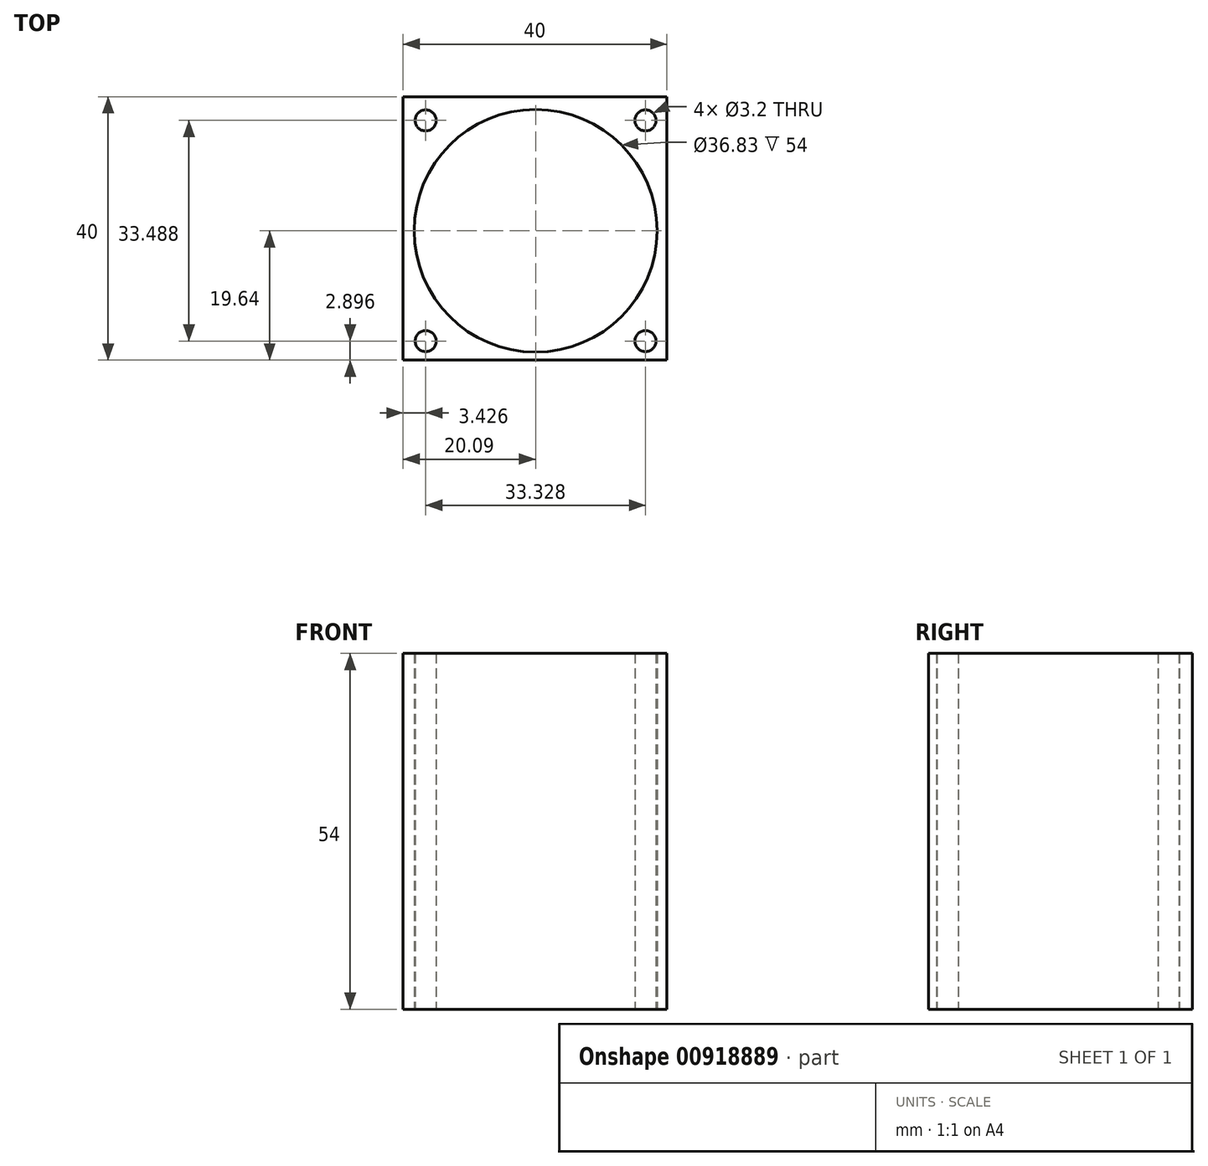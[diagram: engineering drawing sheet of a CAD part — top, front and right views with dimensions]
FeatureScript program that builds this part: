
annotation { "Feature Type Name" : "Feature", "Feature Type Description" : "" }
export const myFeature = defineFeature(function(context is Context, id is Id, definition is map)
    precondition{}
    {
        {
            var Q0;
            Q0=qCreatedBy(makeId("Top.planeOp"),FACE);
            var sketch = newSketch(context, id + "F0", { "sketchPlane" : qUnion([Q0])});
            skLineSegment(sketch, "E0.bottom", {"start": v(-20.09, 20.36) * mm, "end": v(19.91, 20.36) * mm});
            skLineSegment(sketch, "E0.top", {"start": v(-20.09, -19.64) * mm, "end": v(19.91, -19.64) * mm});
            skLineSegment(sketch, "E0.left", {"start": v(-20.09, 20.36) * mm, "end": v(-20.09, -19.64) * mm});
            skLineSegment(sketch, "E0.right", {"start": v(19.91, 20.36) * mm, "end": v(19.91, -19.64) * mm});
            skCircle(sketch, "E1", {"center": v(0, 0) * mm, "radius": 18.42 * mm});
            skCircle(sketch, "E2", {"center": v(-16.66, 16.74) * mm, "radius": 1.6 * mm});
            skCircle(sketch, "E3.MirrorC", {"center": v(16.66, 16.74) * mm, "radius": 1.6 * mm});
            skCircle(sketch, "E4.MirrorC", {"center": v(16.66, -16.74) * mm, "radius": 1.6 * mm});
            skCircle(sketch, "E5.MirrorC", {"center": v(-16.66, -16.74) * mm, "radius": 1.6 * mm});
            skSolve(sketch);
        }
        {
            var Q0;
            Q0=qCreatedBy(makeId("Right.planeOp"),FACE);
            var sketch = newSketch(context, id + "F1", { "sketchPlane" : qUnion([Q0])});
            skLineSegment(sketch, "E6", {"start": v(0, 0) * mm, "end": v(0, -54) * mm});
            skPoint(sketch, "E7", {"position": v(0, -43.88) * mm});
            skSolve(sketch);
        }
        {
            var Q0;
            Q0=makeQuery(id+"F0.imprint","IMPRINT",FACE,{"disambiguationData":[TD([[makeQuery(id+"F0.imprint","IMPRINT",EDGE,{"derivedFrom":sQuery(id+"F0.wireOp",EDGE,"E0.bottom")}),-1.0]])]});
            var Q1;
            Q1=sQuery(id+"F1.wireOp",EDGE,"E6");
            sweep(context, id + "F2", {"profiles" : qUnion([Q0]), "path" : qUnion([Q1])});
        }
    });
